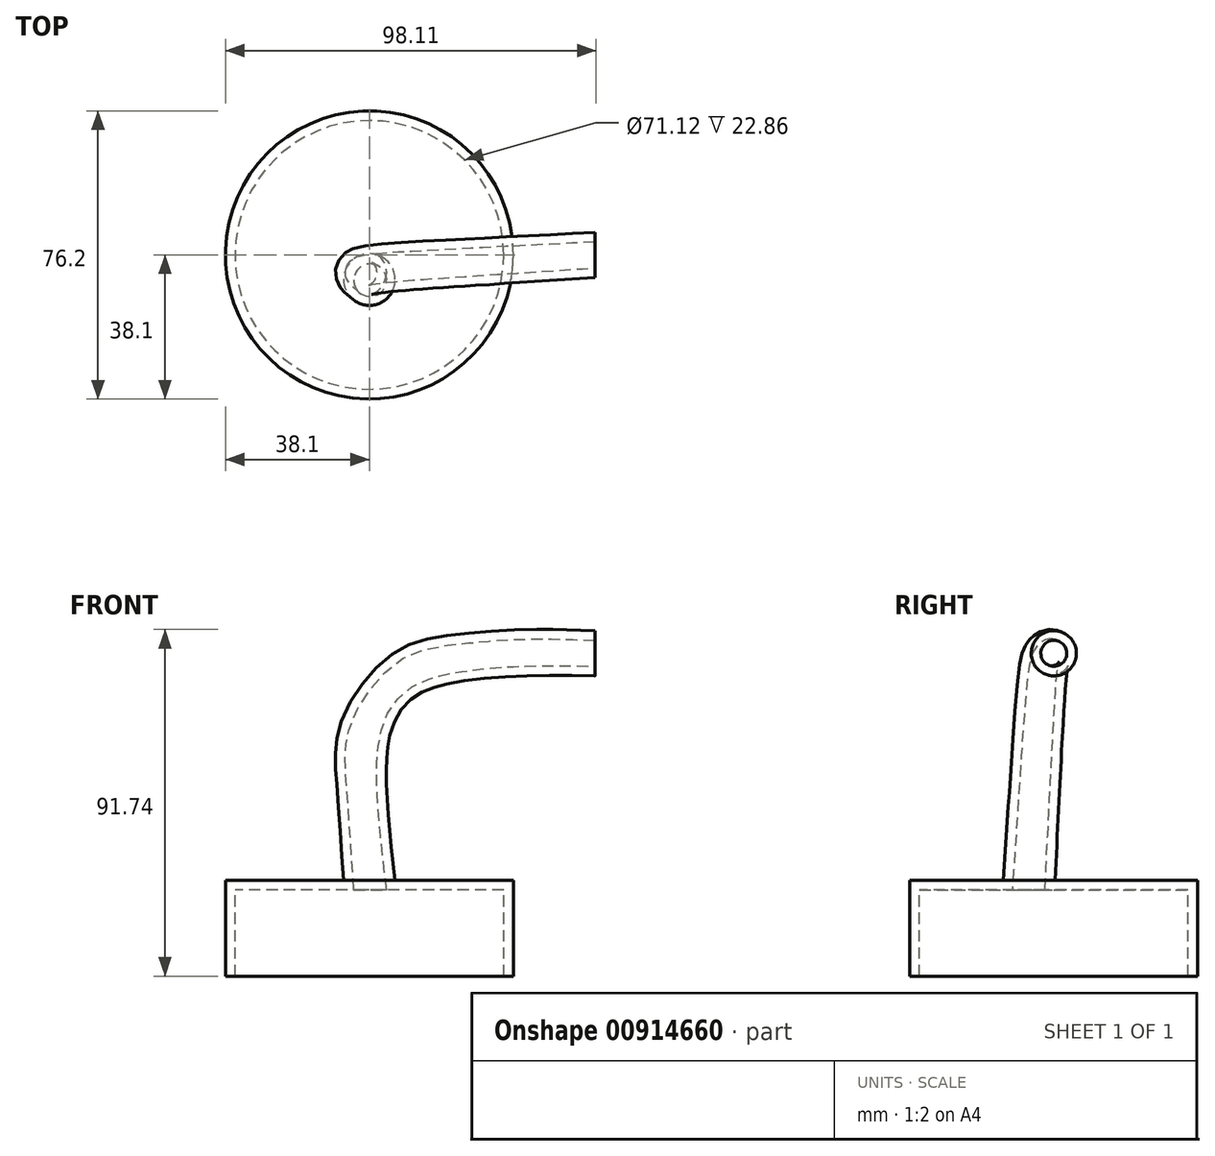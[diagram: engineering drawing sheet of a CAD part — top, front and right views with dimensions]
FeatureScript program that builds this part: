
annotation { "Feature Type Name" : "Feature", "Feature Type Description" : "" }
export const myFeature = defineFeature(function(context is Context, id is Id, definition is map)
    precondition{}
    {
        {
            var Q0;
            Q0=qCreatedBy(makeId("Right.planeOp"),FACE);
            var sketch = newSketch(context, id + "F0", { "sketchPlane" : qUnion([Q0])});
            skLineSegment(sketch, "E0.bottom", {"start": v(0, 15.9) * mm, "end": v(38.1, 15.9) * mm});
            skLineSegment(sketch, "E0.top", {"start": v(0, -9.5) * mm, "end": v(38.1, -9.5) * mm});
            skLineSegment(sketch, "E0.left", {"start": v(0, 15.9) * mm, "end": v(0, -9.5) * mm});
            skLineSegment(sketch, "E0.right", {"start": v(38.1, 15.9) * mm, "end": v(38.1, -9.5) * mm});
            skSolve(sketch);
        }
        {
            var Q0;
            Q0=makeQuery(id+"F0.imprint","IMPRINT",FACE,{"disambiguationData":[TD([[makeQuery(id+"F0.imprint","IMPRINT",EDGE,{"derivedFrom":sQuery(id+"F0.wireOp",EDGE,"E0.bottom")}),-1.0]])]});
            var Q1;
            Q1=sQuery(id+"F0.wireOp",EDGE,"E0.left");
            revolve(context, id + "F1", {"surfaceOperationType" : NewSurfaceOperationType.NEW, "entities" : qUnion([Q0]), "axis" : qUnion([Q1]), "revolveType" : RevolveType.FULL});
        }
        {
            var Q0;
            Q0=qCreatedBy(makeId("Front.planeOp"),FACE);
            var sketch = newSketch(context, id + "F2", { "sketchPlane" : qUnion([Q0])});
            skFitSpline(sketch, "E1", {"points": [v(0, 0) * mm, v(0, 62.1) * mm, v(20.7, 75.15) * mm, v(62.1, 76.26) * mm], "startDerivative": vector(-22.82, 180.83) * mm, "endDerivative": vector(132.1, -4.95) * mm});
            skSolve(sketch);
        }
        {
            var Q0;
            Q0=qCreatedBy(makeId("Right.planeOp"),FACE);
            cPlane(context, id + "F3", {"entities" : qUnion([Q0]), "cplaneType" : CPlaneType.OFFSET, "offset" : 23.37 * mm, "width" : 152.4 * mm, "height" : 152.4 * mm});
        }
        {
            var Q0;
            Q0=qCreatedBy(id+"F3.planeOp",FACE);
            cPlane(context, id + "F4", {"entities" : qUnion([Q0]), "cplaneType" : CPlaneType.OFFSET, "offset" : 36.32 * mm, "width" : 152.4 * mm, "height" : 152.4 * mm});
        }
        {
            var Q0;
            Q0=makeQuery(id+"F1.opRevolve","SWEPT_FACE",FACE,{"disambiguationData":[OSD([sQuery(id+"F0.wireOp",EDGE,"E0.bottom")])]});
            var sketch = newSketch(context, id + "F5", { "sketchPlane" : qUnion([Q0])});
            skCircle(sketch, "E2", {"center": v(0, -6.51) * mm, "radius": 6.83 * mm});
            skSolve(sketch);
        }
        {
            var Q0;
            Q0=qCreatedBy(id+"F4.planeOp",FACE);
            var sketch = newSketch(context, id + "F6", { "sketchPlane" : qUnion([Q0])});
            skCircle(sketch, "E3", {"center": v(0, 75.93) * mm, "radius": 5.98 * mm});
            skSolve(sketch);
        }
        {
            var Q0;
            Q0=sQuery(id+"F2.wireOp",EDGE,"E1");
            var Q2;
            Q2=makeQuery(id+"F5.imprint","IMPRINT",FACE,{"disambiguationData":[TD([[makeQuery(id+"F5.imprint","IMPRINT",EDGE,{"derivedFrom":sQuery(id+"F5.wireOp",EDGE,"E2")}),1.0]])]});
            var Q3;
            Q3=makeQuery(id+"F6.imprint","IMPRINT",FACE,{"disambiguationData":[TD([[makeQuery(id+"F6.imprint","IMPRINT",EDGE,{"derivedFrom":sQuery(id+"F6.wireOp",EDGE,"E3")}),1.0]])]});
            loft(context, id + "F7", {"operationType" : NewBodyOperationType.ADD, "addSections" : true, "spine" : qUnion([Q0]), "sectionCount" : 5, "sheetProfilesArray" : [{ "sheetProfileEntities" : qUnion([Q2]) }, { "sheetProfileEntities" : qUnion([Q3]) }]});
        }
        {
            var Q0;
            Q0=makeQuery(id+"F1.opRevolve","SWEPT_FACE",FACE,{"disambiguationData":[OSD([sQuery(id+"F0.wireOp",EDGE,"E0.top")])]});
            var Q1;
            Q1=makeQuery(id+"F7.opLoft","CAP_FACE",FACE,{"disambiguationData":[OSD([makeQuery(id+"F6.imprint","IMPRINT",FACE,{"disambiguationData":[TD([[makeQuery(id+"F6.imprint","IMPRINT",EDGE,{"derivedFrom":sQuery(id+"F6.wireOp",EDGE,"E3")}),1.0]])]})])],"isStart":true});
            shell(context, id + "F8", {"entities" : qUnion([Q0, Q1]), "thickness" : 2.54 * mm});
        }
    });
